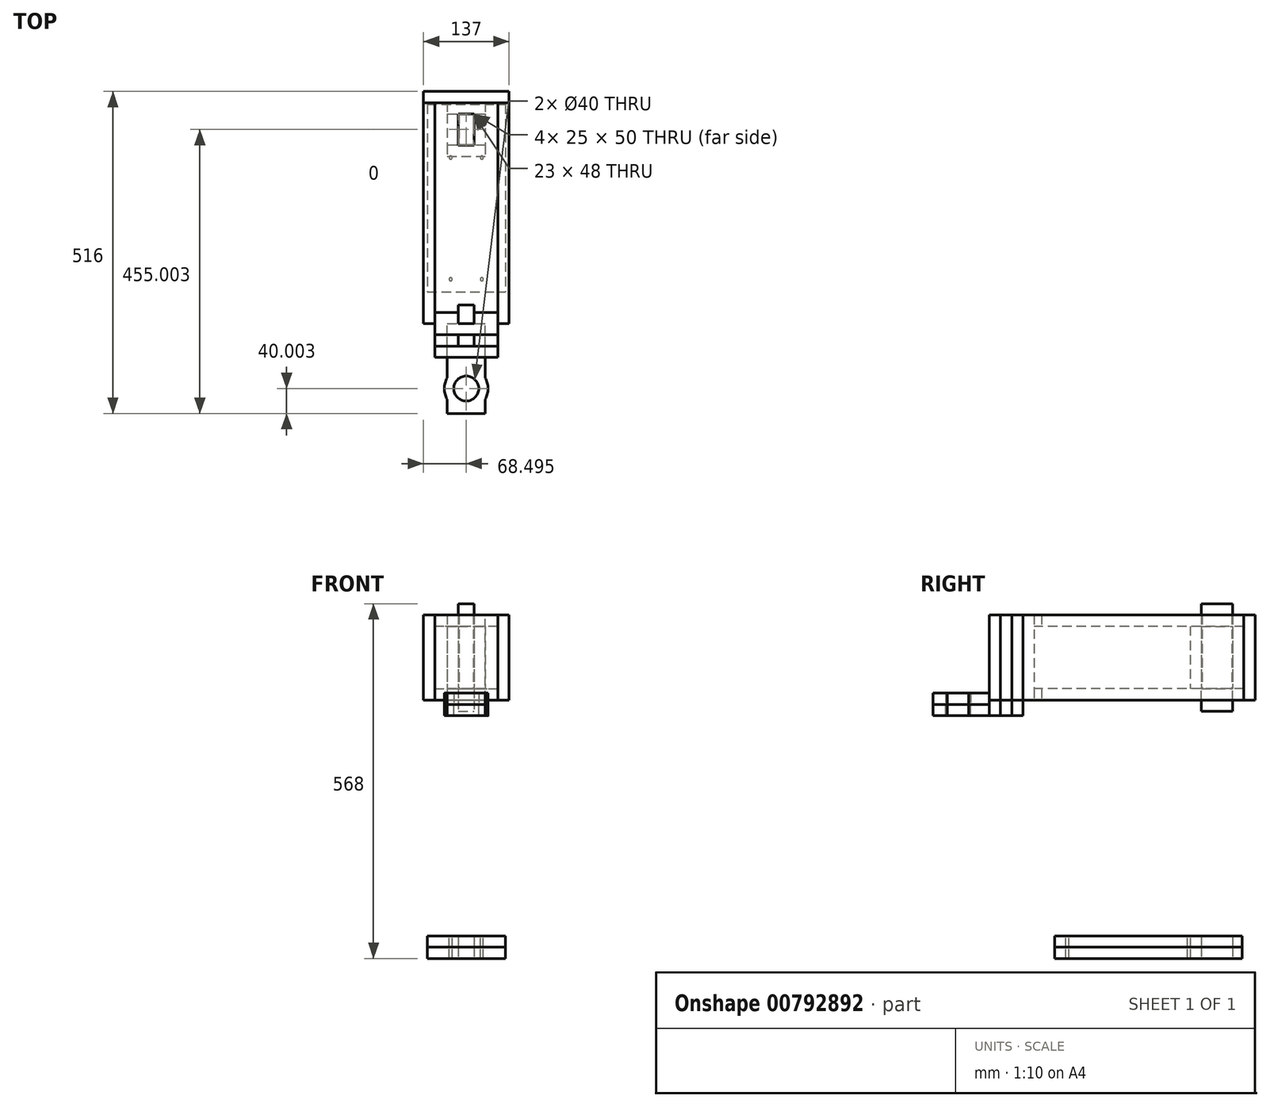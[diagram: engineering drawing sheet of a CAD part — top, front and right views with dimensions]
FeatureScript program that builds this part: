
annotation { "Feature Type Name" : "Feature", "Feature Type Description" : "" }
export const myFeature = defineFeature(function(context is Context, id is Id, definition is map)
    precondition{}
    {
        {
            var Q0;
            Q0=qCreatedBy(makeId("Top.planeOp"),FACE);
            var sketch = newSketch(context, id + "F0", { "sketchPlane" : qUnion([Q0])});
            skLineSegment(sketch, "E0.bottom", {"start": v(-60.34, 180.57) * mm, "end": v(64.66, 180.57) * mm});
            skLineSegment(sketch, "E0.top", {"start": v(-60.34, -119.43) * mm, "end": v(64.66, -119.43) * mm});
            skLineSegment(sketch, "E0.left", {"start": v(-60.34, 180.57) * mm, "end": v(-60.34, -119.43) * mm});
            skLineSegment(sketch, "E0.right", {"start": v(64.66, 180.57) * mm, "end": v(64.66, -119.43) * mm});
            skLineSegment(sketch, "E1.bottom", {"start": v(-10.34, 165.57) * mm, "end": v(14.66, 165.57) * mm});
            skLineSegment(sketch, "E1.top", {"start": v(-10.34, 115.57) * mm, "end": v(14.66, 115.57) * mm});
            skLineSegment(sketch, "E1.left", {"start": v(-10.34, 165.57) * mm, "end": v(-10.34, 115.57) * mm});
            skLineSegment(sketch, "E1.right", {"start": v(14.66, 165.57) * mm, "end": v(14.66, 115.57) * mm});
            skLineSegment(sketch, "E2.0", {"start": v(-9.34, 165.57) * mm, "end": v(-9.34, 115.57) * mm});
            skLineSegment(sketch, "E3.0", {"start": v(-10.34, 116.57) * mm, "end": v(13.66, 116.57) * mm});
            skLineSegment(sketch, "E3.1", {"start": v(13.66, 164.57) * mm, "end": v(13.66, 116.57) * mm});
            skLineSegment(sketch, "E3.2", {"start": v(-10.34, 164.57) * mm, "end": v(13.66, 164.57) * mm});
            skSolve(sketch);
        }
        {
            var Q0;
            Q0=makeQuery(id+"F0.imprint","IMPRINT",FACE,{"disambiguationData":[TD([[makeQuery(id+"F0.imprint","IMPRINT",EDGE,{"derivedFrom":sQuery(id+"F0.wireOp",EDGE,"E0.bottom")}),-1.0]])]});
            extrude(context, id + "F1", {"entities" : qUnion([Q0]), "depth" : 18 * mm, "offsetDistance" : 25 * mm});
        }
        {
            var Q0;
            Q0=makeQuery(id+"F1.opExtrude","CAP_FACE",FACE,{"disambiguationData":[OSD([sQuery(id+"F0.wireOp",EDGE,"E0.bottom"),sQuery(id+"F0.wireOp",EDGE,"E0.top"),sQuery(id+"F0.wireOp",EDGE,"E0.left"),sQuery(id+"F0.wireOp",EDGE,"E0.right"),sQuery(id+"F0.wireOp",EDGE,"E1.bottom"),sQuery(id+"F0.wireOp",EDGE,"E1.top"),sQuery(id+"F0.wireOp",EDGE,"E1.left"),sQuery(id+"F0.wireOp",EDGE,"E1.right")])],"isStart":false});
            extrude(context, id + "F2", {"entities" : qUnion([Q0]), "depth" : 18 * mm, "offsetDistance" : 25 * mm});
        }
        {
            var Q0;
            {var subQ0=sQuery(id+"F0.wireOp",EDGE,"E1.right");Q0=makeQuery(id+"F0.imprint","IMPRINT",FACE,{"disambiguationData":[TD([[makeQuery(id+"F0.imprint","IMPRINT",EDGE,{"derivedFrom":subQ0}),-1.0]])]});}
            var Q1;
            {var subQ0=sQuery(id+"F0.wireOp",EDGE,"E1.left");var subQ1=sQuery(id+"F0.wireOp",EDGE,"E1.bottom");var subQ2=makeQuery(id+"F0.imprint","INTERSECT",VERTEX,{"derivedFrom":[subQ1,subQ0]});Q1=makeQuery(id+"F0.imprint","IMPRINT",FACE,{"disambiguationData":[TD([[makeQuery(id+"F0.imprint","IMPRINT",EDGE,{"disambiguationData":[TD([[subQ2,-1.0]])],"derivedFrom":subQ1}),-1.0]])]});}
            var Q2;
            {var subQ0=sQuery(id+"F0.wireOp",EDGE,"E3.0");var subQ1=sQuery(id+"F0.wireOp",EDGE,"E1.left");var subQ2=makeQuery(id+"F0.imprint","INTERSECT",VERTEX,{"derivedFrom":[subQ1,subQ0]});Q2=makeQuery(id+"F0.imprint","IMPRINT",FACE,{"disambiguationData":[TD([[makeQuery(id+"F0.imprint","IMPRINT",EDGE,{"disambiguationData":[TD([[subQ2,1.0]])],"derivedFrom":subQ1}),1.0]])]});}
            var Q3;
            {var subQ0=sQuery(id+"F0.wireOp",EDGE,"E1.left");var subQ1=sQuery(id+"F0.wireOp",EDGE,"E1.top");var subQ2=makeQuery(id+"F0.imprint","INTERSECT",VERTEX,{"derivedFrom":[subQ1,subQ0]});Q3=makeQuery(id+"F0.imprint","IMPRINT",FACE,{"disambiguationData":[TD([[makeQuery(id+"F0.imprint","IMPRINT",EDGE,{"disambiguationData":[TD([[subQ2,-1.0]])],"derivedFrom":subQ1}),1.0]])]});}
            extrude(context, id + "F3", {"entities" : qUnion([Q0, Q1, Q2, Q3]), "depth" : 550 * mm, "offsetDistance" : 25 * mm});
        }
        {
            var Q0;
            Q0=makeQuery(id+"F2.opExtrude","CAP_FACE",FACE,{"disambiguationData":[OSD([sQuery(id+"F0.wireOp",EDGE,"E0.bottom"),sQuery(id+"F0.wireOp",EDGE,"E0.top"),sQuery(id+"F0.wireOp",EDGE,"E0.left"),sQuery(id+"F0.wireOp",EDGE,"E0.right"),sQuery(id+"F0.wireOp",EDGE,"E1.bottom"),sQuery(id+"F0.wireOp",EDGE,"E1.top"),sQuery(id+"F0.wireOp",EDGE,"E1.left"),sQuery(id+"F0.wireOp",EDGE,"E1.right")])],"isStart":false});
            var sketch = newSketch(context, id + "F4", { "sketchPlane" : qUnion([Q0])});
            skCircle(sketch, "E4", {"center": v(-22.84, -99.43) * mm, "radius": 2.5 * mm});
            skCircle(sketch, "E5", {"center": v(27.16, -99.43) * mm, "radius": 2.5 * mm});
            skCircle(sketch, "E6", {"center": v(27.16, 95.57) * mm, "radius": 2.5 * mm});
            skCircle(sketch, "E7", {"center": v(-22.84, 95.57) * mm, "radius": 2.5 * mm});
            skSolve(sketch);
        }
        {
            var Q0;
            Q0 = qSketchRegion(id + "F4", true);
            extrude(context, id + "F5", {"entities" : qUnion([Q0]), "operationType" : NewBodyOperationType.REMOVE, "endBound" : BoundingType.THROUGH_ALL, "oppositeDirection" : true, "depth" : 25 * mm, "offsetDistance" : 25 * mm});
        }
        {
            var Q0;
            Q0=makeQuery(id+"F2.opExtrude","CAP_FACE",FACE,{"disambiguationData":[OSD([sQuery(id+"F0.wireOp",EDGE,"E0.bottom"),sQuery(id+"F0.wireOp",EDGE,"E0.top"),sQuery(id+"F0.wireOp",EDGE,"E0.left"),sQuery(id+"F0.wireOp",EDGE,"E0.right"),sQuery(id+"F0.wireOp",EDGE,"E1.bottom"),sQuery(id+"F0.wireOp",EDGE,"E1.top"),sQuery(id+"F0.wireOp",EDGE,"E1.left"),sQuery(id+"F0.wireOp",EDGE,"E1.right")])],"isStart":false});
            cPlane(context, id + "F6", {"entities" : qUnion([Q0]), "cplaneType" : CPlaneType.OFFSET, "offset" : 396 * mm, "width" : 150 * mm, "height" : 150 * mm});
        }
        {
            var Q0;
            Q0=qCreatedBy(id+"F6.planeOp",FACE);
            var sketch = newSketch(context, id + "F7", { "sketchPlane" : qUnion([Q0])});
            skLineSegment(sketch, "E8.0", {"start": v(-28.34, 183.57) * mm, "end": v(-28.34, 97.57) * mm});
            skLineSegment(sketch, "E8.1", {"start": v(-28.34, 183.57) * mm, "end": v(32.66, 183.57) * mm});
            skLineSegment(sketch, "E8.2", {"start": v(32.66, 183.57) * mm, "end": v(32.66, 97.57) * mm});
            skLineSegment(sketch, "E8.3", {"start": v(-28.34, 97.57) * mm, "end": v(32.66, 97.57) * mm});
            skLineSegment(sketch, "E9", {"start": v(-28.34, 165.57) * mm, "end": v(32.66, 165.57) * mm});
            skLineSegment(sketch, "E10", {"start": v(32.66, 115.57) * mm, "end": v(-28.34, 115.57) * mm});
            skLineSegment(sketch, "E11", {"start": v(-10.34, 183.57) * mm, "end": v(-10.34, 97.57) * mm});
            skLineSegment(sketch, "E12", {"start": v(14.66, 97.57) * mm, "end": v(14.66, 183.57) * mm});
            skSolve(sketch);
        }
        {
            var Q0;
            {var subQ0=sQuery(id+"F7.wireOp",EDGE,"E9");var subQ1=sQuery(id+"F7.wireOp",EDGE,"E8.0");var subQ2=makeQuery(id+"F7.imprint","INTERSECT",VERTEX,{"derivedFrom":[subQ1,subQ0]});Q0=makeQuery(id+"F7.imprint","IMPRINT",FACE,{"disambiguationData":[TD([[makeQuery(id+"F7.imprint","IMPRINT",EDGE,{"disambiguationData":[TD([[subQ2,-1.0]])],"derivedFrom":subQ1}),1.0]])]});}
            var Q1;
            {var subQ0=sQuery(id+"F7.wireOp",EDGE,"E9");var subQ1=sQuery(id+"F7.wireOp",EDGE,"E8.2");var subQ2=makeQuery(id+"F7.imprint","INTERSECT",VERTEX,{"derivedFrom":[subQ1,subQ0]});Q1=makeQuery(id+"F7.imprint","IMPRINT",FACE,{"disambiguationData":[TD([[makeQuery(id+"F7.imprint","IMPRINT",EDGE,{"disambiguationData":[TD([[subQ2,-1.0]])],"derivedFrom":subQ1}),-1.0]])]});}
            extrude(context, id + "F8", {"entities" : qUnion([Q0, Q1]), "depth" : 100 * mm, "offsetDistance" : 25 * mm});
        }
        {
            var Q0;
            {var subQ0=sQuery(id+"F7.wireOp",EDGE,"E8.3");var subQ1=sQuery(id+"F7.wireOp",EDGE,"E8.0");var subQ2=makeQuery(id+"F7.imprint","INTERSECT",VERTEX,{"derivedFrom":[subQ1,subQ0]});Q0=makeQuery(id+"F7.imprint","IMPRINT",FACE,{"disambiguationData":[TD([[makeQuery(id+"F7.imprint","IMPRINT",EDGE,{"disambiguationData":[TD([[subQ2,1.0]])],"derivedFrom":subQ1}),1.0]])]});}
            var Q1;
            {var subQ0=sQuery(id+"F7.wireOp",EDGE,"E11");var subQ1=sQuery(id+"F7.wireOp",EDGE,"E8.3");var subQ2=makeQuery(id+"F7.imprint","INTERSECT",VERTEX,{"derivedFrom":[subQ1,subQ0]});Q1=makeQuery(id+"F7.imprint","IMPRINT",FACE,{"disambiguationData":[TD([[makeQuery(id+"F7.imprint","IMPRINT",EDGE,{"disambiguationData":[TD([[subQ2,-1.0]])],"derivedFrom":subQ1}),1.0]])]});}
            var Q2;
            {var subQ0=sQuery(id+"F7.wireOp",EDGE,"E8.3");var subQ1=sQuery(id+"F7.wireOp",EDGE,"E8.2");var subQ2=makeQuery(id+"F7.imprint","INTERSECT",VERTEX,{"derivedFrom":[subQ1,subQ0]});Q2=makeQuery(id+"F7.imprint","IMPRINT",FACE,{"disambiguationData":[TD([[makeQuery(id+"F7.imprint","IMPRINT",EDGE,{"disambiguationData":[TD([[subQ2,1.0]])],"derivedFrom":subQ1}),-1.0]])]});}
            var Q3;
            {var subQ0=sQuery(id+"F7.wireOp",EDGE,"E8.2");var subQ1=sQuery(id+"F7.wireOp",EDGE,"E8.1");var subQ2=makeQuery(id+"F7.imprint","INTERSECT",VERTEX,{"derivedFrom":[subQ1,subQ0]});Q3=makeQuery(id+"F7.imprint","IMPRINT",FACE,{"disambiguationData":[TD([[makeQuery(id+"F7.imprint","IMPRINT",EDGE,{"disambiguationData":[TD([[subQ2,1.0]])],"derivedFrom":subQ1}),-1.0]])]});}
            var Q4;
            {var subQ0=sQuery(id+"F7.wireOp",EDGE,"E11");var subQ1=sQuery(id+"F7.wireOp",EDGE,"E8.1");var subQ2=makeQuery(id+"F7.imprint","INTERSECT",VERTEX,{"derivedFrom":[subQ1,subQ0]});Q4=makeQuery(id+"F7.imprint","IMPRINT",FACE,{"disambiguationData":[TD([[makeQuery(id+"F7.imprint","IMPRINT",EDGE,{"disambiguationData":[TD([[subQ2,-1.0]])],"derivedFrom":subQ1}),-1.0]])]});}
            var Q5;
            {var subQ0=sQuery(id+"F7.wireOp",EDGE,"E8.1");var subQ1=sQuery(id+"F7.wireOp",EDGE,"E8.0");var subQ2=makeQuery(id+"F7.imprint","INTERSECT",VERTEX,{"derivedFrom":[subQ1,subQ0]});Q5=makeQuery(id+"F7.imprint","IMPRINT",FACE,{"disambiguationData":[TD([[makeQuery(id+"F7.imprint","IMPRINT",EDGE,{"disambiguationData":[TD([[subQ2,-1.0]])],"derivedFrom":subQ1}),1.0]])]});}
            extrude(context, id + "F9", {"entities" : qUnion([Q0, Q1, Q2, Q3, Q4, Q5]), "depth" : 100 * mm, "offsetDistance" : 25 * mm});
        }
        {
            var Q0;
            Q0=qCreatedBy(id+"F6.planeOp",FACE);
            var sketch = newSketch(context, id + "F10", { "sketchPlane" : qUnion([Q0])});
            skLineSegment(sketch, "E13.bottom", {"start": v(-48.34, 183.57) * mm, "end": v(52.66, 183.57) * mm});
            skLineSegment(sketch, "E13.top", {"start": v(-48.34, -152.43) * mm, "end": v(52.66, -152.43) * mm});
            skLineSegment(sketch, "E13.left", {"start": v(-48.34, 183.57) * mm, "end": v(-48.34, -152.43) * mm});
            skLineSegment(sketch, "E13.right", {"start": v(52.66, 183.57) * mm, "end": v(52.66, -152.43) * mm});
            skSolve(sketch);
        }
        {
            var Q0;
            Q0=makeQuery(id+"F10.imprint","IMPRINT",FACE,{"disambiguationData":[TD([[makeQuery(id+"F10.imprint","IMPRINT",EDGE,{"derivedFrom":sQuery(id+"F10.wireOp",EDGE,"E13.bottom")}),-1.0]])]});
            extrude(context, id + "F11", {"entities" : qUnion([Q0]), "oppositeDirection" : true, "depth" : 18 * mm, "offsetDistance" : 25 * mm});
        }
        {
            var Q0;
            Q0=makeQuery(id+"F9.opExtrude","CAP_FACE",FACE,{"disambiguationData":[OSD([sQuery(id+"F7.wireOp",EDGE,"E8.0"),sQuery(id+"F7.wireOp",EDGE,"E8.2"),sQuery(id+"F7.wireOp",EDGE,"E8.3"),sQuery(id+"F7.wireOp",EDGE,"E10")])],"isStart":false});
            cPlane(context, id + "F12", {"entities" : qUnion([Q0]), "cplaneType" : CPlaneType.OFFSET, "offset" : 0 * mm, "width" : 150 * mm, "height" : 150 * mm});
        }
        {
            var Q0;
            Q0=qCreatedBy(id+"F12.planeOp",FACE);
            var sketch = newSketch(context, id + "F13", { "sketchPlane" : qUnion([Q0])});
            skLineSegment(sketch, "E14.bottom", {"start": v(52.66, 183.57) * mm, "end": v(-48.34, 183.57) * mm});
            skLineSegment(sketch, "E14.top", {"start": v(52.66, -152.43) * mm, "end": v(-48.34, -152.43) * mm});
            skLineSegment(sketch, "E14.left", {"start": v(52.66, 183.57) * mm, "end": v(52.66, -152.43) * mm});
            skLineSegment(sketch, "E14.right", {"start": v(-48.34, 183.57) * mm, "end": v(-48.34, -152.43) * mm});
            skLineSegment(sketch, "E15", {"start": v(-48.34, 115.57) * mm, "end": v(52.66, 115.57) * mm});
            skLineSegment(sketch, "E16", {"start": v(-48.34, 165.57) * mm, "end": v(52.66, 165.57) * mm});
            skLineSegment(sketch, "E17", {"start": v(14.66, 115.57) * mm, "end": v(14.66, 165.57) * mm});
            skLineSegment(sketch, "E18", {"start": v(14.66, 165.57) * mm, "end": v(-10.34, 165.57) * mm});
            skLineSegment(sketch, "E19", {"start": v(-10.34, 165.57) * mm, "end": v(-10.34, 115.57) * mm});
            skSolve(sketch);
        }
        {
            var Q0;
            Q0 = qSketchRegion(id + "F13", true);
            extrude(context, id + "F14", {"entities" : qUnion([Q0]), "depth" : 18 * mm, "offsetDistance" : 25 * mm});
        }
        {
            var Q0;
            Q0=makeQuery(id+"F14.opExtrude","SWEPT_FACE",FACE,{"disambiguationData":[OSD([sQuery(id+"F13.wireOp",EDGE,"E14.top")])]});
            var sketch = newSketch(context, id + "F15", { "sketchPlane" : qUnion([Q0])});
            skLineSegment(sketch, "E20.bottom", {"start": v(-48.34, 550) * mm, "end": v(52.66, 550) * mm});
            skLineSegment(sketch, "E20.top", {"start": v(-48.34, 414) * mm, "end": v(52.66, 414) * mm});
            skLineSegment(sketch, "E20.left", {"start": v(-48.34, 550) * mm, "end": v(-48.34, 414) * mm});
            skLineSegment(sketch, "E20.right", {"start": v(52.66, 550) * mm, "end": v(52.66, 414) * mm});
            skSolve(sketch);
        }
        {
            var Q0;
            {var subQ0=sQuery(id+"F15.wireOp",EDGE,"E20.top");Q0=makeQuery(id+"F15.imprint","IMPRINT",FACE,{"disambiguationData":[TD([[makeQuery(id+"F15.imprint","IMPRINT",EDGE,{"derivedFrom":subQ0}),1.0]])]});}
            var Q1;
            {var subQ0=sQuery(id+"F15.wireOp",EDGE,"E20.bottom");Q1=makeQuery(id+"F15.imprint","IMPRINT",FACE,{"disambiguationData":[TD([[makeQuery(id+"F15.imprint","IMPRINT",EDGE,{"derivedFrom":subQ0}),1.0]])]});}
            extrude(context, id + "F16", {"entities" : qUnion([Q0, Q1]), "depth" : 18 * mm, "offsetDistance" : 25 * mm});
        }
        {
            var Q0;
            {var subQ0=sQuery(id+"F7.wireOp",EDGE,"E11");var subQ1=sQuery(id+"F7.wireOp",EDGE,"E9");var subQ2=makeQuery(id+"F7.imprint","INTERSECT",VERTEX,{"derivedFrom":[subQ1,subQ0]});Q0=makeQuery(id+"F7.imprint","IMPRINT",FACE,{"disambiguationData":[TD([[makeQuery(id+"F7.imprint","IMPRINT",EDGE,{"disambiguationData":[TD([[subQ2,-1.0]])],"derivedFrom":subQ1}),-1.0]])]});}
            extrude(context, id + "F17", {"entities" : qUnion([Q0]), "operationType" : NewBodyOperationType.REMOVE, "endBound" : BoundingType.THROUGH_ALL, "oppositeDirection" : true, "depth" : 25 * mm, "offsetDistance" : 25 * mm});
        }
        {
            var Q0;
            Q0=makeQuery(id+"F16.opExtrude","CAP_FACE",FACE,{"disambiguationData":[OSD([sQuery(id+"F15.wireOp",EDGE,"E20.bottom"),sQuery(id+"F15.wireOp",EDGE,"E20.top"),sQuery(id+"F15.wireOp",EDGE,"E20.left"),sQuery(id+"F15.wireOp",EDGE,"E20.right")])],"isStart":false});
            var sketch = newSketch(context, id + "F18", { "sketchPlane" : qUnion([Q0])});
            skLineSegment(sketch, "E21.bottom", {"start": v(-48.34, 550) * mm, "end": v(-28.34, 550) * mm});
            skLineSegment(sketch, "E21.top", {"start": v(-48.34, 414) * mm, "end": v(-28.34, 414) * mm});
            skLineSegment(sketch, "E21.left", {"start": v(-48.34, 550) * mm, "end": v(-48.34, 414) * mm});
            skLineSegment(sketch, "E21.right", {"start": v(-28.34, 550) * mm, "end": v(-28.34, 414) * mm});
            skLineSegment(sketch, "E22.bottom", {"start": v(32.66, 414) * mm, "end": v(52.66, 414) * mm});
            skLineSegment(sketch, "E22.top", {"start": v(32.66, 550) * mm, "end": v(52.66, 550) * mm});
            skLineSegment(sketch, "E22.left", {"start": v(32.66, 414) * mm, "end": v(32.66, 550) * mm});
            skLineSegment(sketch, "E22.right", {"start": v(52.66, 414) * mm, "end": v(52.66, 550) * mm});
            skLineSegment(sketch, "E23.bottom", {"start": v(-10.34, 550) * mm, "end": v(14.66, 550) * mm});
            skLineSegment(sketch, "E23.top", {"start": v(-10.34, 414) * mm, "end": v(14.66, 414) * mm});
            skLineSegment(sketch, "E23.left", {"start": v(-10.34, 550) * mm, "end": v(-10.34, 414) * mm});
            skLineSegment(sketch, "E23.right", {"start": v(14.66, 550) * mm, "end": v(14.66, 414) * mm});
            skSolve(sketch);
        }
        {
            var Q0;
            Q0=makeQuery(id+"F18.imprint","IMPRINT",FACE,{"disambiguationData":[TD([[makeQuery(id+"F18.imprint","IMPRINT",EDGE,{"derivedFrom":sQuery(id+"F18.wireOp",EDGE,"E23.bottom")}),-1.0]])]});
            var Q1;
            Q1=makeQuery(id+"F18.imprint","IMPRINT",FACE,{"disambiguationData":[TD([[makeQuery(id+"F18.imprint","IMPRINT",EDGE,{"derivedFrom":sQuery(id+"F18.wireOp",EDGE,"E23.bottom")}),1.0]])]});
            extrude(context, id + "F19", {"entities" : qUnion([Q0, Q1]), "operationType" : NewBodyOperationType.REMOVE, "oppositeDirection" : true, "depth" : 30 * mm, "offsetDistance" : 25 * mm});
        }
        {
            var Q0;
            Q0=makeQuery(id+"F18.imprint","IMPRINT",FACE,{"disambiguationData":[TD([[makeQuery(id+"F18.imprint","IMPRINT",EDGE,{"derivedFrom":sQuery(id+"F18.wireOp",EDGE,"E21.bottom")}),1.0]])]});
            var Q1;
            Q1=makeQuery(id+"F18.imprint","IMPRINT",FACE,{"disambiguationData":[TD([[makeQuery(id+"F18.imprint","IMPRINT",EDGE,{"derivedFrom":sQuery(id+"F18.wireOp",EDGE,"E22.bottom")}),1.0]])]});
            extrude(context, id + "F20", {"entities" : qUnion([Q0, Q1]), "depth" : 18 * mm, "offsetDistance" : 25 * mm});
        }
        {
            var Q0;
            Q0=makeQuery(id+"F20.opExtrude","CAP_FACE",FACE,{"disambiguationData":[OSD([sQuery(id+"F18.wireOp",EDGE,"E21.bottom"),sQuery(id+"F18.wireOp",EDGE,"E21.top"),sQuery(id+"F18.wireOp",EDGE,"E21.left"),sQuery(id+"F18.wireOp",EDGE,"E21.right")])],"isStart":false});
            var sketch = newSketch(context, id + "F21", { "sketchPlane" : qUnion([Q0])});
            skLineSegment(sketch, "E24.bottom", {"start": v(-48.34, 550) * mm, "end": v(-10.34, 550) * mm});
            skLineSegment(sketch, "E24.top", {"start": v(-48.34, 414) * mm, "end": v(-10.34, 414) * mm});
            skLineSegment(sketch, "E24.left", {"start": v(-48.34, 550) * mm, "end": v(-48.34, 414) * mm});
            skLineSegment(sketch, "E24.right", {"start": v(-10.34, 550) * mm, "end": v(-10.34, 414) * mm});
            skLineSegment(sketch, "E25.bottom", {"start": v(52.66, 550) * mm, "end": v(14.66, 550) * mm});
            skLineSegment(sketch, "E25.top", {"start": v(52.66, 414) * mm, "end": v(14.66, 414) * mm});
            skLineSegment(sketch, "E25.left", {"start": v(52.66, 550) * mm, "end": v(52.66, 414) * mm});
            skLineSegment(sketch, "E25.right", {"start": v(14.66, 550) * mm, "end": v(14.66, 414) * mm});
            skSolve(sketch);
        }
        {
            var Q0;
            {var subQ0=sQuery(id+"F21.wireOp",EDGE,"E24.left");Q0=makeQuery(id+"F21.imprint","IMPRINT",FACE,{"disambiguationData":[TD([[makeQuery(id+"F21.imprint","IMPRINT",EDGE,{"derivedFrom":subQ0}),1.0]])]});}
            var Q1;
            {var subQ2=sQuery(id+"F21.wireOp",EDGE,"E24.right");Q1=makeQuery(id+"F21.imprint","IMPRINT",FACE,{"disambiguationData":[TD([[makeQuery(id+"F21.imprint","IMPRINT",EDGE,{"derivedFrom":subQ2}),-1.0]])]});}
            var Q2;
            Q2=makeQuery(id+"F21.imprint","IMPRINT",FACE,{"disambiguationData":[TD([[makeQuery(id+"F21.imprint","IMPRINT",EDGE,{"derivedFrom":sQuery(id+"F21.wireOp",EDGE,"E25.bottom")}),1.0]])]});
            extrude(context, id + "F22", {"entities" : qUnion([Q0, Q1, Q2]), "depth" : 18 * mm, "offsetDistance" : 25 * mm});
        }
        {
            var Q0;
            {var subQ0=sQuery(id+"F18.wireOp",EDGE,"E21.right");Q0=makeQuery(id+"F18.imprint","IMPRINT",FACE,{"disambiguationData":[TD([[makeQuery(id+"F18.imprint","IMPRINT",EDGE,{"derivedFrom":subQ0}),1.0]])]});}
            var Q1;
            Q1=makeQuery(id+"F18.imprint","IMPRINT",FACE,{"disambiguationData":[TD([[makeQuery(id+"F18.imprint","IMPRINT",EDGE,{"derivedFrom":sQuery(id+"F18.wireOp",EDGE,"E23.bottom")}),1.0]])]});
            var Q2;
            {var subQ0=sQuery(id+"F18.wireOp",EDGE,"E22.left");Q2=makeQuery(id+"F18.imprint","IMPRINT",FACE,{"disambiguationData":[TD([[makeQuery(id+"F18.imprint","IMPRINT",EDGE,{"derivedFrom":subQ0}),1.0]])]});}
            extrude(context, id + "F23", {"entities" : qUnion([Q0, Q1, Q2]), "depth" : 17.9 * mm, "offsetDistance" : 25 * mm});
        }
        {
            var Q0;
            Q0=makeQuery(id+"F23.opExtrude","SWEPT_FACE",FACE,{"disambiguationData":[OSD([sQuery(id+"F15.wireOp",EDGE,"E20.top"),sQuery(id+"F18.wireOp",EDGE,"E23.top")])]});
            extrude(context, id + "F24", {"entities" : qUnion([Q0]), "operationType" : NewBodyOperationType.ADD, "depth" : 25 * mm, "offsetDistance" : 25 * mm});
        }
        {
            var Q0;
            {var subQ0=sQuery(id+"F18.wireOp",EDGE,"E23.top");var subQ1=sQuery(id+"F15.wireOp",EDGE,"E20.top");Q0=makeQuery(id+"F24.boolean.opBoolean","MERGE",FACE,{"derivedFrom":[makeQuery(id+"F23.opExtrude","CAP_FACE",FACE,{"disambiguationData":[OSD([sQuery(id+"F15.wireOp",EDGE,"E20.bottom"),subQ1,sQuery(id+"F18.wireOp",EDGE,"E21.right"),sQuery(id+"F18.wireOp",EDGE,"E22.left"),sQuery(id+"F18.wireOp",EDGE,"E23.bottom"),subQ0])],"isStart":false}),makeQuery(id+"F24.opExtrude","SWEPT_FACE",FACE,{"disambiguationData":[OSD([subQ1,subQ0]),TDD([makeQuery(id+"F23.opExtrude","CAP_EDGE",EDGE,{"disambiguationData":[OSD([subQ1,subQ0])],"isStart":false})])]})]});}
            var sketch = newSketch(context, id + "F25", { "sketchPlane" : qUnion([Q0])});
            skLineSegment(sketch, "E26.bottom", {"start": v(32.66, 389) * mm, "end": v(-28.34, 389) * mm});
            skLineSegment(sketch, "E26.top", {"start": v(32.66, 414) * mm, "end": v(-28.34, 414) * mm});
            skLineSegment(sketch, "E26.left", {"start": v(32.66, 389) * mm, "end": v(32.66, 414) * mm});
            skLineSegment(sketch, "E26.right", {"start": v(-28.34, 389) * mm, "end": v(-28.34, 414) * mm});
            skSolve(sketch);
        }
        {
            var Q0;
            Q0=makeQuery(id+"F25.imprint","IMPRINT",FACE,{"disambiguationData":[TD([[makeQuery(id+"F25.imprint","IMPRINT",EDGE,{"derivedFrom":sQuery(id+"F25.wireOp",EDGE,"E26.bottom")}),1.0]])]});
            extrude(context, id + "F26", {"entities" : qUnion([Q0]), "depth" : 18 * mm, "offsetDistance" : 25 * mm});
        }
        {
            var Q0;
            {var subQ0=sQuery(id+"F18.wireOp",EDGE,"E23.top");var subQ1=sQuery(id+"F15.wireOp",EDGE,"E20.top");Q0=makeQuery(id+"F24.boolean.opBoolean","MERGE",FACE,{"derivedFrom":[makeQuery(id+"F23.opExtrude","CAP_FACE",FACE,{"disambiguationData":[OSD([sQuery(id+"F15.wireOp",EDGE,"E20.bottom"),subQ1,sQuery(id+"F18.wireOp",EDGE,"E21.right"),sQuery(id+"F18.wireOp",EDGE,"E22.left"),sQuery(id+"F18.wireOp",EDGE,"E23.bottom"),subQ0])],"isStart":false}),makeQuery(id+"F24.opExtrude","SWEPT_FACE",FACE,{"disambiguationData":[OSD([subQ1,subQ0]),TDD([makeQuery(id+"F23.opExtrude","CAP_EDGE",EDGE,{"disambiguationData":[OSD([subQ1,subQ0])],"isStart":false})])]})]});}
            var sketch = newSketch(context, id + "F27", { "sketchPlane" : qUnion([Q0])});
            skLineSegment(sketch, "E27.bottom", {"start": v(-10.34, 550) * mm, "end": v(14.66, 550) * mm});
            skLineSegment(sketch, "E27.top", {"start": v(-10.34, 414) * mm, "end": v(14.66, 414) * mm});
            skLineSegment(sketch, "E27.left", {"start": v(-10.34, 550) * mm, "end": v(-10.34, 414) * mm});
            skLineSegment(sketch, "E27.right", {"start": v(14.66, 550) * mm, "end": v(14.66, 414) * mm});
            skSolve(sketch);
        }
        {
            var Q0;
            Q0=makeQuery(id+"F27.imprint","IMPRINT",FACE,{"disambiguationData":[TD([[makeQuery(id+"F27.imprint","IMPRINT",EDGE,{"derivedFrom":sQuery(id+"F27.wireOp",EDGE,"E27.bottom")}),1.0]])]});
            extrude(context, id + "F28", {"entities" : qUnion([Q0]), "depth" : 18 * mm, "offsetDistance" : 25 * mm});
        }
        {
            var Q0;
            Q0=makeQuery(id+"F22.opExtrude","CAP_FACE",FACE,{"disambiguationData":[OSD([sQuery(id+"F21.wireOp",EDGE,"E24.bottom"),sQuery(id+"F21.wireOp",EDGE,"E24.top"),sQuery(id+"F21.wireOp",EDGE,"E24.left"),sQuery(id+"F21.wireOp",EDGE,"E24.right")])],"isStart":false});
            var sketch = newSketch(context, id + "F29", { "sketchPlane" : qUnion([Q0])});
            skLineSegment(sketch, "E28", {"start": v(-48.34, 550) * mm, "end": v(52.66, 550) * mm});
            skLineSegment(sketch, "E29", {"start": v(52.66, 550) * mm, "end": v(52.66, 414) * mm});
            skLineSegment(sketch, "E30", {"start": v(52.66, 414) * mm, "end": v(32.66, 414) * mm});
            skLineSegment(sketch, "E31", {"start": v(32.66, 414) * mm, "end": v(32.66, 389) * mm});
            skLineSegment(sketch, "E32", {"start": v(32.66, 389) * mm, "end": v(-28.34, 389) * mm});
            skLineSegment(sketch, "E33", {"start": v(-28.34, 389) * mm, "end": v(-28.34, 414) * mm});
            skLineSegment(sketch, "E34", {"start": v(-28.34, 414) * mm, "end": v(-48.34, 414) * mm});
            skLineSegment(sketch, "E35", {"start": v(-48.34, 414) * mm, "end": v(-48.34, 550) * mm});
            skSolve(sketch);
        }
        {
            var Q0;
            {var subQ0=sQuery(id+"F29.wireOp",EDGE,"E29");Q0=makeQuery(id+"F29.imprint","IMPRINT",FACE,{"disambiguationData":[TD([[makeQuery(id+"F29.imprint","IMPRINT",EDGE,{"derivedFrom":subQ0}),-1.0]])]});}
            var Q1;
            {var subQ2=sQuery(id+"F29.wireOp",EDGE,"E34");Q1=makeQuery(id+"F29.imprint","IMPRINT",FACE,{"disambiguationData":[TD([[makeQuery(id+"F29.imprint","IMPRINT",EDGE,{"derivedFrom":subQ2}),1.0]])]});}
            extrude(context, id + "F30", {"entities" : qUnion([Q0, Q1]), "depth" : 18 * mm, "offsetDistance" : 25 * mm});
        }
        {
            var Q0;
            Q0=makeQuery(id+"F30.opExtrude","CAP_FACE",FACE,{"disambiguationData":[OSD([sQuery(id+"F29.wireOp",EDGE,"E28"),sQuery(id+"F29.wireOp",EDGE,"E29"),sQuery(id+"F29.wireOp",EDGE,"E30"),sQuery(id+"F29.wireOp",EDGE,"E31"),sQuery(id+"F29.wireOp",EDGE,"E32"),sQuery(id+"F29.wireOp",EDGE,"E33"),sQuery(id+"F29.wireOp",EDGE,"E34"),sQuery(id+"F29.wireOp",EDGE,"E35")])],"isStart":false});
            var sketch = newSketch(context, id + "F31", { "sketchPlane" : qUnion([Q0])});
            skLineSegment(sketch, "E36.bottom", {"start": v(-28.34, 389) * mm, "end": v(32.66, 389) * mm});
            skLineSegment(sketch, "E36.top", {"start": v(-28.34, 407) * mm, "end": v(32.66, 407) * mm});
            skLineSegment(sketch, "E36.left", {"start": v(-28.34, 389) * mm, "end": v(-28.34, 407) * mm});
            skLineSegment(sketch, "E36.right", {"start": v(32.66, 389) * mm, "end": v(32.66, 407) * mm});
            skSolve(sketch);
        }
        {
            var Q0;
            Q0=makeQuery(id+"F31.imprint","IMPRINT",FACE,{"disambiguationData":[TD([[makeQuery(id+"F31.imprint","IMPRINT",EDGE,{"derivedFrom":sQuery(id+"F31.wireOp",EDGE,"E36.bottom")}),-1.0]])]});
            extrude(context, id + "F32", {"entities" : qUnion([Q0]), "depth" : 90 * mm, "offsetDistance" : 25 * mm});
        }
        {
            var Q0;
            Q0=makeQuery(id+"F32.opExtrude","SWEPT_FACE",FACE,{"disambiguationData":[OSD([sQuery(id+"F31.wireOp",EDGE,"E36.top")])]});
            var sketch = newSketch(context, id + "F33", { "sketchPlane" : qUnion([Q0])});
            skCircle(sketch, "E37", {"center": v(2.16, -274.43) * mm, "radius": 20 * mm});
            skCircle(sketch, "E38", {"center": v(2.16, -274.43) * mm, "radius": 35 * mm});
            skLineSegment(sketch, "E39.bottom", {"start": v(0.66, -314.43) * mm, "end": v(3.66, -314.43) * mm});
            skLineSegment(sketch, "E39.top", {"start": v(0.66, -274.43) * mm, "end": v(3.66, -274.43) * mm});
            skSolve(sketch);
        }
        {
            var Q0;
            {var subQ0=sQuery(id+"F33.wireOp",EDGE,"E38");var subQ1=makeQuery(id+"F32.opExtrude","SWEPT_EDGE",EDGE,{"disambiguationData":[OSD([sQuery(id+"F29.wireOp",EDGE,"E31"),sQuery(id+"F31.wireOp",EDGE,"E36.top"),sQuery(id+"F31.wireOp",EDGE,"E36.right")])]});var subQ2=makeQuery(id+"F33.imprint","INTERSECT",VERTEX,{"disambiguationData":[OD(0.0)],"derivedFrom":[subQ1,subQ0]});Q0=makeQuery(id+"F33.imprint","IMPRINT",FACE,{"disambiguationData":[TD([[makeQuery(id+"F33.imprint","IMPRINT",EDGE,{"disambiguationData":[TD([[subQ2,1.0]])],"derivedFrom":subQ0}),1.0]])]});}
            var Q1;
            {var subQ0=sQuery(id+"F33.wireOp",EDGE,"E38");var subQ1=makeQuery(id+"F32.opExtrude","SWEPT_EDGE",EDGE,{"disambiguationData":[OSD([sQuery(id+"F29.wireOp",EDGE,"E33"),sQuery(id+"F31.wireOp",EDGE,"E36.top"),sQuery(id+"F31.wireOp",EDGE,"E36.left")])]});var subQ2=makeQuery(id+"F33.imprint","INTERSECT",VERTEX,{"disambiguationData":[OD(0.0)],"derivedFrom":[subQ1,subQ0]});Q1=makeQuery(id+"F33.imprint","IMPRINT",FACE,{"disambiguationData":[TD([[makeQuery(id+"F33.imprint","IMPRINT",EDGE,{"disambiguationData":[TD([[subQ2,-1.0]])],"derivedFrom":subQ0}),1.0]])]});}
            var Q2;
            Q2=makeQuery(id+"F33.imprint","IMPRINT",FACE,{"disambiguationData":[TD([[makeQuery(id+"F33.imprint","IMPRINT",EDGE,{"derivedFrom":sQuery(id+"F33.wireOp",EDGE,"E37")}),-1.0]])]});
            extrude(context, id + "F34", {"entities" : qUnion([Q0, Q1, Q2]), "operationType" : NewBodyOperationType.ADD, "oppositeDirection" : true, "depth" : 18 * mm, "offsetDistance" : 25 * mm});
        }
        {
            var Q0;
            Q0=makeQuery(id+"F33.imprint","IMPRINT",FACE,{"disambiguationData":[TD([[makeQuery(id+"F33.imprint","IMPRINT",EDGE,{"derivedFrom":sQuery(id+"F33.wireOp",EDGE,"E37")}),1.0]])]});
            extrude(context, id + "F35", {"entities" : qUnion([Q0]), "operationType" : NewBodyOperationType.REMOVE, "oppositeDirection" : true, "depth" : 24 * mm, "offsetDistance" : 25 * mm});
        }
        {
            var Q0;
            {var subQ0=sQuery(id+"F33.wireOp",EDGE,"E38");var subQ1=makeQuery(id+"F32.opExtrude","SWEPT_EDGE",EDGE,{"disambiguationData":[OSD([sQuery(id+"F29.wireOp",EDGE,"E33"),sQuery(id+"F31.wireOp",EDGE,"E36.top"),sQuery(id+"F31.wireOp",EDGE,"E36.left")])]});var subQ2=makeQuery(id+"F33.imprint","INTERSECT",VERTEX,{"disambiguationData":[OD(0.0)],"derivedFrom":[subQ1,subQ0]});Q0=makeQuery(id+"F33.imprint","IMPRINT",FACE,{"disambiguationData":[TD([[makeQuery(id+"F33.imprint","IMPRINT",EDGE,{"disambiguationData":[TD([[subQ2,-1.0]])],"derivedFrom":subQ0}),1.0]])]});}
            var Q1;
            {var subQ0=sQuery(id+"F33.wireOp",EDGE,"E38");var subQ1=makeQuery(id+"F32.opExtrude","SWEPT_EDGE",EDGE,{"disambiguationData":[OSD([sQuery(id+"F29.wireOp",EDGE,"E31"),sQuery(id+"F31.wireOp",EDGE,"E36.top"),sQuery(id+"F31.wireOp",EDGE,"E36.right")])]});var subQ2=makeQuery(id+"F33.imprint","INTERSECT",VERTEX,{"disambiguationData":[OD(0.0)],"derivedFrom":[subQ1,subQ0]});Q1=makeQuery(id+"F33.imprint","IMPRINT",FACE,{"disambiguationData":[TD([[makeQuery(id+"F33.imprint","IMPRINT",EDGE,{"disambiguationData":[TD([[subQ2,1.0]])],"derivedFrom":subQ0}),1.0]])]});}
            extrude(context, id + "F36", {"entities" : qUnion([Q0, Q1]), "operationType" : NewBodyOperationType.ADD, "oppositeDirection" : true, "depth" : 18 * mm, "offsetDistance" : 25 * mm});
        }
        {
            var Q0;
            {var subQ0=sQuery(id+"F33.wireOp",EDGE,"E38");var subQ1=sQuery(id+"F31.wireOp",EDGE,"E36.top");Q0=makeQuery(id+"F36.boolean.opBoolean","MERGE",FACE,{"derivedFrom":[makeQuery(id+"F32.opExtrude","SWEPT_FACE",FACE,{"disambiguationData":[OSD([subQ1])]}),makeQuery(id+"F36.opExtrude","CAP_FACE",FACE,{"disambiguationData":[OSD([sQuery(id+"F29.wireOp",EDGE,"E33"),subQ1,sQuery(id+"F31.wireOp",EDGE,"E36.left"),subQ0])],"isStart":true}),makeQuery(id+"F36.opExtrude","CAP_FACE",FACE,{"disambiguationData":[OSD([sQuery(id+"F29.wireOp",EDGE,"E31"),subQ1,sQuery(id+"F31.wireOp",EDGE,"E36.right"),subQ0])],"isStart":true})]});}
            extrude(context, id + "F37", {"entities" : qUnion([Q0]), "depth" : 18 * mm, "offsetDistance" : 25 * mm});
        }
        {
            var Q0;
            Q0=makeQuery(id+"F14.opExtrude","SWEPT_FACE",FACE,{"disambiguationData":[OSD([sQuery(id+"F13.wireOp",EDGE,"E14.right")])]});
            var sketch = newSketch(context, id + "F38", { "sketchPlane" : qUnion([Q0])});
            skLineSegment(sketch, "E40.bottom", {"start": v(-183.57, 550) * mm, "end": v(152.43, 550) * mm});
            skLineSegment(sketch, "E40.top", {"start": v(-183.57, 414) * mm, "end": v(152.43, 414) * mm});
            skLineSegment(sketch, "E40.left", {"start": v(-183.57, 550) * mm, "end": v(-183.57, 414) * mm});
            skLineSegment(sketch, "E40.right", {"start": v(152.43, 550) * mm, "end": v(152.43, 414) * mm});
            skLineSegment(sketch, "E41.bottom", {"start": v(-183.57, 550) * mm, "end": v(170.43, 550) * mm});
            skLineSegment(sketch, "E41.top", {"start": v(-183.57, 414) * mm, "end": v(170.43, 414) * mm});
            skLineSegment(sketch, "E41.right", {"start": v(170.43, 550) * mm, "end": v(170.43, 414) * mm});
            skSolve(sketch);
        }
        {
            var Q0;
            Q0 = qSketchRegion(id + "F38", true);
            extrude(context, id + "F39", {"entities" : qUnion([Q0]), "depth" : 18 * mm, "offsetDistance" : 25 * mm});
        }
        {
            var Q0;
            Q0=makeQuery(id+"F14.opExtrude","SWEPT_FACE",FACE,{"disambiguationData":[OSD([sQuery(id+"F13.wireOp",EDGE,"E14.left")])]});
            var sketch = newSketch(context, id + "F40", { "sketchPlane" : qUnion([Q0])});
            skLineSegment(sketch, "E42.bottom", {"start": v(183.57, 550) * mm, "end": v(-170.43, 550) * mm});
            skLineSegment(sketch, "E42.top", {"start": v(183.57, 414) * mm, "end": v(-170.43, 414) * mm});
            skLineSegment(sketch, "E42.left", {"start": v(183.57, 550) * mm, "end": v(183.57, 414) * mm});
            skLineSegment(sketch, "E42.right", {"start": v(-170.43, 550) * mm, "end": v(-170.43, 414) * mm});
            skSolve(sketch);
        }
        {
            var Q0;
            Q0 = qSketchRegion(id + "F40", true);
            extrude(context, id + "F41", {"entities" : qUnion([Q0]), "depth" : 18 * mm, "offsetDistance" : 25 * mm});
        }
        {
            var Q0;
            Q0=makeQuery(id+"F14.opExtrude","SWEPT_FACE",FACE,{"disambiguationData":[OSD([sQuery(id+"F13.wireOp",EDGE,"E14.bottom")])]});
            var sketch = newSketch(context, id + "F42", { "sketchPlane" : qUnion([Q0])});
            skLineSegment(sketch, "E43.bottom", {"start": v(-70.66, 550) * mm, "end": v(66.34, 550) * mm});
            skLineSegment(sketch, "E43.top", {"start": v(-70.66, 414) * mm, "end": v(66.34, 414) * mm});
            skLineSegment(sketch, "E43.left", {"start": v(-70.66, 550) * mm, "end": v(-70.66, 414) * mm});
            skLineSegment(sketch, "E43.right", {"start": v(66.34, 550) * mm, "end": v(66.34, 414) * mm});
            skSolve(sketch);
        }
        {
            var Q0;
            Q0 = qSketchRegion(id + "F42", true);
            extrude(context, id + "F43", {"entities" : qUnion([Q0]), "depth" : 18 * mm, "offsetDistance" : 25 * mm});
        }
        {
            var Q0;
            Q0=makeQuery(id+"F14.opExtrude","CAP_FACE",FACE,{"disambiguationData":[OSD([sQuery(id+"F13.wireOp",EDGE,"E14.bottom"),sQuery(id+"F13.wireOp",EDGE,"E14.top"),sQuery(id+"F13.wireOp",EDGE,"E14.left"),sQuery(id+"F13.wireOp",EDGE,"E14.right"),sQuery(id+"F13.wireOp",EDGE,"E15"),sQuery(id+"F13.wireOp",EDGE,"E17"),sQuery(id+"F13.wireOp",EDGE,"E18"),sQuery(id+"F13.wireOp",EDGE,"E19")])],"isStart":false});
            var sketch = newSketch(context, id + "F44", { "sketchPlane" : qUnion([Q0])});
            skLineSegment(sketch, "E44.bottom", {"start": v(-10.34, 165.57) * mm, "end": v(14.66, 165.57) * mm});
            skLineSegment(sketch, "E44.top", {"start": v(-10.34, 115.57) * mm, "end": v(14.66, 115.57) * mm});
            skLineSegment(sketch, "E44.left", {"start": v(-10.34, 165.57) * mm, "end": v(-10.34, 115.57) * mm});
            skLineSegment(sketch, "E44.right", {"start": v(14.66, 165.57) * mm, "end": v(14.66, 115.57) * mm});
            skLineSegment(sketch, "E45.bottom", {"start": v(-28.8, 97.57) * mm, "end": v(32.66, 97.57) * mm});
            skLineSegment(sketch, "E45.top", {"start": v(-28.8, 183.57) * mm, "end": v(32.66, 183.57) * mm});
            skLineSegment(sketch, "E45.left", {"start": v(-28.8, 97.57) * mm, "end": v(-28.8, 183.57) * mm});
            skLineSegment(sketch, "E45.right", {"start": v(32.66, 97.57) * mm, "end": v(32.66, 183.57) * mm});
            skSolve(sketch);
        }
        {
            var Q0;
            Q0=makeQuery(id+"F44.imprint","IMPRINT",FACE,{"disambiguationData":[TD([[makeQuery(id+"F44.imprint","IMPRINT",EDGE,{"derivedFrom":sQuery(id+"F44.wireOp",EDGE,"E44.bottom")}),-1.0]])]});
            extrude(context, id + "F45", {"entities" : qUnion([Q0]), "depth" : 18 * mm, "offsetDistance" : 25 * mm});
        }
        {
            var Q0;
            Q0=makeQuery(id+"F45.opExtrude","SWEPT_BODY",BODY,{"disambiguationData":[OSD([sQuery(id+"F44.wireOp",EDGE,"E44.bottom"),sQuery(id+"F44.wireOp",EDGE,"E44.top"),sQuery(id+"F44.wireOp",EDGE,"E44.left"),sQuery(id+"F44.wireOp",EDGE,"E44.right"),sQuery(id+"F44.wireOp",EDGE,"E45.bottom"),sQuery(id+"F44.wireOp",EDGE,"E45.top"),sQuery(id+"F44.wireOp",EDGE,"E45.left"),sQuery(id+"F44.wireOp",EDGE,"E45.right")])]});
            transform(context, id + "F46", {"entities" : qUnion([Q0]), "transformType" : TransformType.TRANSLATION_3D, "dx" : 0 * mm, "dy" : 0 * mm, "dz" : -153.7 * mm, "makeCopy" : true});
        }
    });
